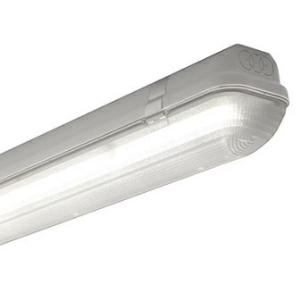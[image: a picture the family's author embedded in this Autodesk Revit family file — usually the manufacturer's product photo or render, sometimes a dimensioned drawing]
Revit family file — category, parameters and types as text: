
# Revit family: 3f_filippi_-_3f_linda_3f_filippi_-_58589_-_3f_linda_led_1x24w_ep_l1270
name_source: partatom
category: Lighting Fixtures
units: mm (PartAtom-declared; Revit-internal decimal feet)

## family parameters
Cut with Voids When Loaded = No
Host = Face
Light Source = No
Part Type = Normal
Room Calculation Point = No
Round Connector Dimension = Use Diameter
Shared = No

## types (1)
- 3F Filippi - 3F Linda (1 x LED, 4065 lm, 29 W, 4000 K)
    Apparent Load = 29 VA
    Approval mark = ENEC
    CIE Flux Codes = 44 77 94 97 100
    Color Rendering = 80
    Color Temperature = 4000 K
    Control Gear = Electronic ballast
    Default Elevation = 1800 mm
    Description = ILLUMINOTECHNICAL
Luminous efficiency 100% (DLOR 97%, ULOR 3%).
Initial luminous flux of the luminaire 4065 lm.
Emergency luminaire luminous flux BLF 14.3%.
Controlled symmetric distribution.
Installation Interdistance Transv.D = 1.77 x hu - Long.D = 1.17 x hu.
Tabular UGR (CIE 117 - 4H-8H; S=0.25H; 70/50/20): RUG 22 - 22.9.
Beam angle: 109° - 64°.
Luminous efficacy 140 lm/W.
Lifetime (L93/B10): 30000 h. (tq+25°C)
Lifetime (L90/B10): 50000 h. (tq+25°C)
Lifetime (L85/B10): 80000 h. (tq+25°C)
Lifetime (L80/B10): 100000 h. (tq+25°C)
Sudden decreased luminous flux after 50000 hours: 0% (C0).
Photobiological safety in compliance with IEC/TR 62778: RG0 risk exempt, (IEC 62471).
In compliance with IEC/EN 62722-2-1 - IEC/EN 62717 standards.

SOURCE
Linear LED module 24W/840.
Energy efficiency class (UE 2019/2020 - UE 2019/2015): D.
CIE 13.3 Colour rendering index: CRI >80 (R9 <50%).
IES TM-30 Fidelity Index: Rf = 84 Rg = 95.
CCT nominal colour temperature 4000 K.
Colour initial tolerance (MacAdam): SDCM 3.

MECHANICAL
Self-extinguishing V2 polycarbonate housing, injection moulded, RAL 7035 grey.
Ecologic anti-aging injected sealing gasket.
Diffuser in self-extinguishing V2 polycarbonate, photo-engraved interior, UV stabilised, injection moulded with smooth outer surface, tamper-proof opening.
Gear-holder reflector in hot-dip galvanised steel, painted with white polyester base.
Snug fit safety snap-lock clips for diffuser mounting in stainless steel, screwdriver opening.
Fixing brackets in stainless steel.
Possibility for technicians to access the interior of the luminaire.
Luminaire with limited surface temperature. - D - (EN 60598-2-24)
Dimensions: 1270x100 mm, height 100 mm. Weight 2.434 kg.
IP66 protection degree.
Mechanical strength to impacts IK10 (20 joule).
Glow-wire test resistance 850°C.

ELECTRICAL
Halogen Free electronic wiring 230V-50/60Hz, power factor 0.90, THD <25%, constant output current, SELV, class I, 1 driver.
Power of the luminaire 29 W.
CE - IEC 60598-1 - EN 60598-1.
EP maintained emergency wiring on board, 1h duration, 24h recharge; compliant with EN 60598-2-22, excluding high risk areas.
SAFE FLICKER: PstLM=<1 and SVM=<0.4 (IEC TR 61547-1 and IEC TR 63158), to ensure a more comfortable and safe light.
Ambient temperature from +5°C to +25°C.
Temperature class T6 max 85°C.
Relative humidity UR: <85%.

INSTALLATION
Ceiling / Suspended / Wall.
All accessories dedicated to this product are available on the Catalog and on our website www.3F-Filippi.com.

APPLICATIONS
Suitable product for food production plants (HACCP), IFS (Food Version 6), BRC (GSFS Food Version 7).
Dry, dusty indoor environments, subject to occasional water splashes.
Virtually shatterproof polycarbonate compatibly with the fumes / atmospheres that compromise the elasticity of plastic materials.
Not suitable for installation on surfaces subject to important vibrations, exposed to weather conditions, on ropes or poles.
Suitable for illumination of public car parks and parking grounds referred to DIN 67528:2018-04.

WARNING
Fixture not suitable for cold stores with an ambient temperature <5°C and/or relative humidity >85%.
Luminaire designed for disposal/recycling at end-of-life.
Replaceable (LED only) light source by a professional. Replaceable control gear by a professional.
    Height = 100 mm  [stored 0.328084 ft]
    Lamp = 1 x LED
    Lamp Light Flux = 4065 lm
    Lamp Power = 29 W
    Lamp count = 1
    Length = 1270 mm
    Lifetime = 50000 h
    Luminous efficacy = 140 lm/W
    Manufacturer = 3F Filippi
    ModVariant = No
    Model = 3F Filippi - 58589 - 3F Linda LED 1x24W EP L1270
    Mounting Place = Ceiling
    Mounting Type = Pendant
    Number of Poles = 1
    OnlyDefault = Yes
    Power Factor = 1
    Product Name = 3F Filippi - 3F Linda
    Product group = pendant luminaire
    ProductGroupID = 9
    Protection Class = Protection class I
    Protection Degree = IP 66
    RLX_Detail_Level = 1
    RLX_Emergency_Light_Flux = 0 lm
    RLX_Emergency_Type = 0
    RLX_Emergency_Type_DB = No
    RlxData = <blob elided: 68301 chars, md5=7a572bba>
    Socket = socket
    Standby Power = 0 W
    System Light Flux = 4065 lm
    System Power = 29 W
    Type Comments = Product without accessories
    Type Image = 3ffilippi_3f_linda_led_1x.jpg
    URL = http://relux.com
    VarID = ---
    Voltage = 0 V
    Weight = 0.00 kg
    Width = 100 mm  [stored 0.328084 ft]

note: [stored X ft] marks values corroborated as IEEE doubles in the binary element streams (Revit-internal decimal feet)

## geometry (parser evidence)
native form markers: Blend x4, Sweep x9
no freeform markers — native parametric forms only
